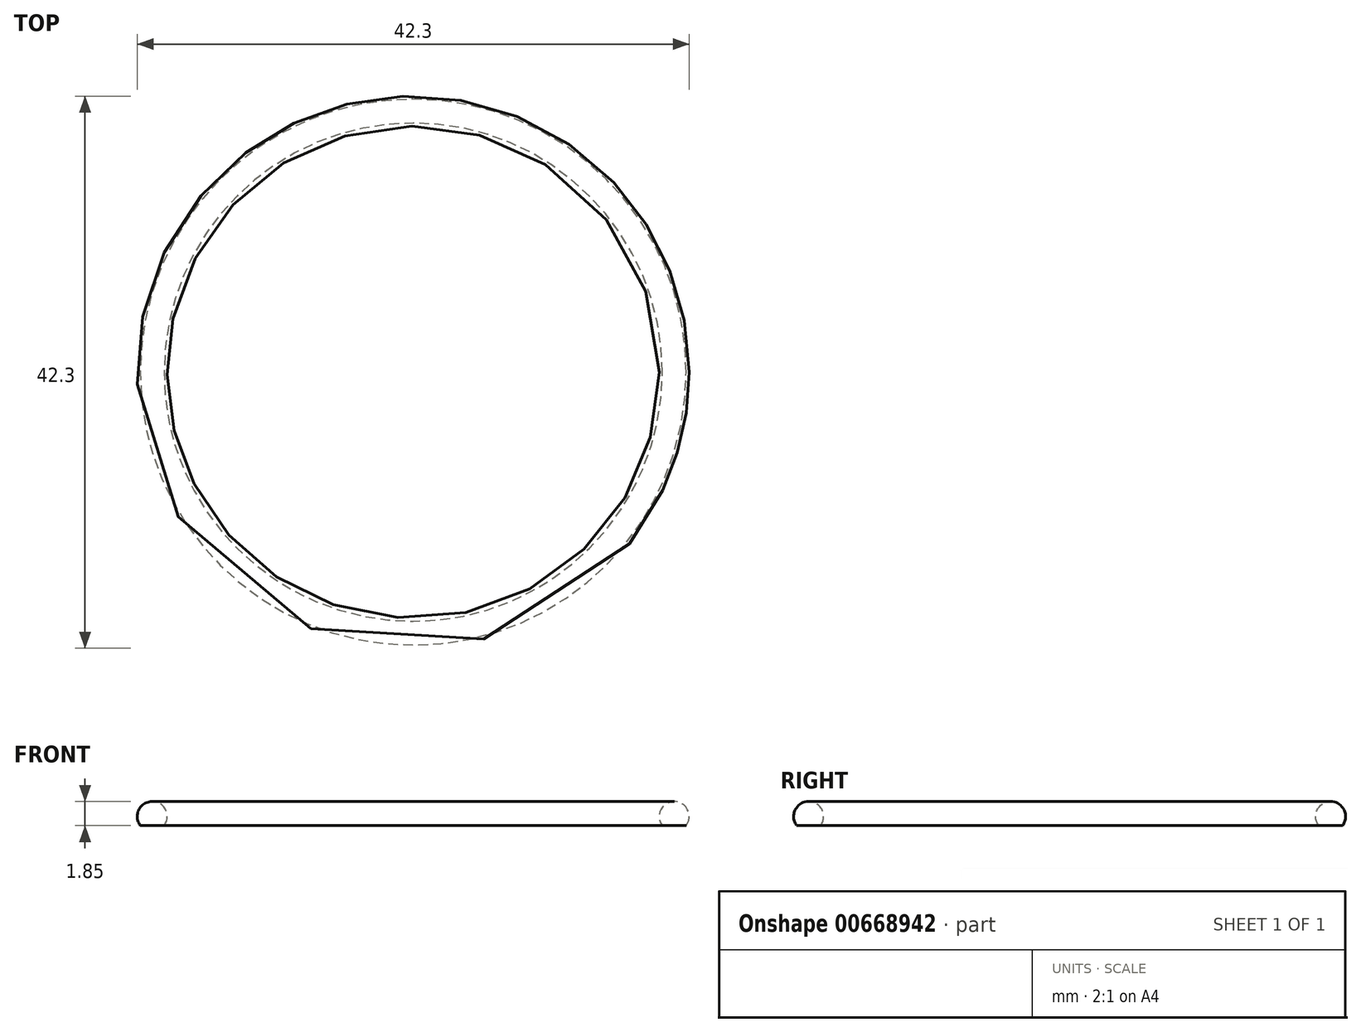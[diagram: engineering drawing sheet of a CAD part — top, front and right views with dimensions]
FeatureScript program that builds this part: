
annotation { "Feature Type Name" : "Feature", "Feature Type Description" : "" }
export const myFeature = defineFeature(function(context is Context, id is Id, definition is map)
    precondition{}
    {
        {
            var Q0;
            Q0=qCreatedBy(makeId("Front.planeOp"),FACE);
            var sketch = newSketch(context, id + "F0", { "sketchPlane" : qUnion([Q0])});
            skLineSegment(sketch, "E0", {"start": v(0, 20.03) * mm, "end": v(0, -19.4) * mm, "construction": true});
            skLineSegment(sketch, "E1", {"start": v(-87.12, 0) * mm, "end": v(19.84, 0) * mm, "construction": true});
            skArc(sketch, "E2", {"start": v(-19.09, 0) * mm, "mid": v(-20, 1.85) * mm, "end": v(-20.91, 0) * mm});
            skLineSegment(sketch, "E3", {"start": v(-20.91, 0) * mm, "end": v(-19.09, 0) * mm});
            skSolve(sketch);
        }
        {
            var Q0;
            Q0=makeQuery(id+"F0.imprint","IMPRINT",FACE,{"disambiguationData":[TD([[makeQuery(id+"F0.imprint","IMPRINT",EDGE,{"derivedFrom":sQuery(id+"F0.wireOp",EDGE,"E2")}),1.0]])]});
            var Q1;
            Q1=sQuery(id+"F0.wireOp",EDGE,"E0");
            revolve(context, id + "F1", {"entities" : qUnion([Q0]), "axis" : qUnion([Q1]), "revolveType" : RevolveType.FULL});
        }
    });
